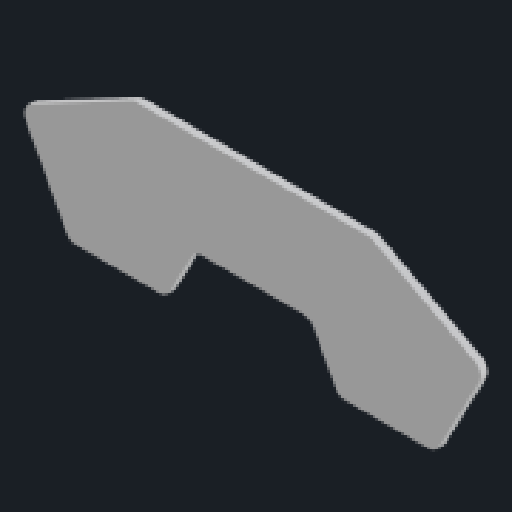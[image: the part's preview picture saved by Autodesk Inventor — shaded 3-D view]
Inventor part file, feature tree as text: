
AUTODESK INVENTOR PART (.ipt)
format: ipt  version: 2023 (Build 270158000, 158)  size: 168,448 bytes
history: native  units: in
note: dims shown in document units (in); Inventor stores cm internally (conversion verified against a paired STEP export)
features: extrude x2, sketch x2
ambient origin geometry x8: Origin, YZ Plane, XZ Plane, XY Plane, X Axis, Y Axis, Z Axis, Center Point
bodies: Body1 (feature_tree)
feature tree (4):
  extrude  "Extrusion2"  Depth=0.9033in
  extrude  "Extrusion3"  Depth=0.0394in
  sketch  "Sketch2"  dims[d8=0.0787in d9=0.0in d10=0.9033in]
  sketch  "Sketch3"  dims[d11=0.68in d12=0.0394in d13=0.6566in d15=0.6566in d16=0.35in d17=0.0in d18=0.0in]
